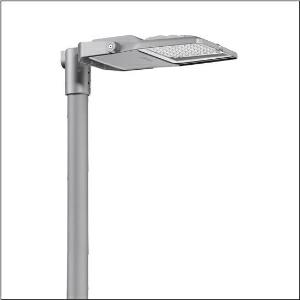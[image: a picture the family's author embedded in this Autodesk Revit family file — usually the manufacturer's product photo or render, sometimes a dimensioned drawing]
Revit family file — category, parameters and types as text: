
# Revit family: floodlight_fl_21_iq_mini___pl52_5xa7771b2d3a_cd8f
name_source: partatom
category: Lighting Fixtures
units: mm (PartAtom-declared; Revit-internal decimal feet)

## family parameters
Cut with Voids When Loaded = No
Host = Face
Light Source = No
Part Type = Normal
Room Calculation Point = No
Round Connector Dimension = Use Diameter
Shared = No

## types (1)
- --- (1 x LED, 6240 lm, 45.5 W, 3000K)
    Apparent Load = 46 VA
    CIE Flux Codes = 26 60 98 100 100
    Color Rendering = 70
    Color Temperature = 3000K
    Default Elevation = 1800 mm
    Description = Floodlight FL 21 iQ mini, floodlight, primary light control with lens, of PMMA, primary optical cover: protective disc, of toughened safety glass, transparent, light distribution: PL52, light emission: direct distribution, installation type: surface-mounted, LED, High Power LED, rated luminous flux: 6.240lm, luminous efficacy: 137lm/W, light colour: 730, colour temperature: 3000K, control: Auto-Match, Temp-Guard, Lumen-Switch, Night-Set, Smart-Wire, Light-Fading, Desk-Remote (wireless, voltage-free reading and setting of iQ features in the workshop via application-optimized NFC function/RFID function), optimised constant luminous flux control (CLO 2.0), with terminal, 6-pole, mains connection: 220..240V, AC, 50/60Hz, start of lifetime: 46W, end of service life: 48W, reduction: 22W, luminaire housing, of diecast aluminium, powder-coated, Siteco® metallic grey (DB 702S), corrosivity category C5 mid according to DIN EN ISO 12944, sealing non-destructively replaceable, please order mast flange separately, mast bracket, of steel, galvanised, powder-coated, Siteco® metallic grey (DB 702S), protection rating (complete): IP66, insulation class (complete): insulation class II (safety insulation), certification: CE, ENEC, VDE, protection symbol: D, impact resistance: IK08, permissible operating ambient temperature: -40..+40°C, permissible operating ambient temperature for outdoor applications: -40..+50°C, standard: DIN EN 12944, LABS conformity tested according to VDMA 24364:2018-05, packaging unit: 1 piece

Light Distribution: PL52
    Height = 70 mm
    Lamp = 1 x LED
    Lamp Light Flux = 6240 lm
    Lamp Power = 45.5 W
    Lamp count = 1
    Length = 485 mm
    Luminous efficacy = 137 lm/W
    Manufacturer = Siteco
    ModVariant = No
    Model = 5XA7771B2D3A
    Number of Poles = 1
    OnlyDefault = Yes
    Power Factor = 1
    Product Name = Floodlight FL 21 iQ mini | PL52
    Product group = floodlight | pylon annexe
    ProductGroupID = 6200
    Protection Class = Protection class II
    Protection Degree = IP 66
    RLX_Detail_Level = 1
    RLX_Emergency_Light_Flux = 0 lm
    RLX_Emergency_Type = 0
    RLX_Emergency_Type_DB = No
    RlxData = <blob elided: 101385 chars, md5=539fc8cc>
    Socket = socket
    Standby Power = 0 W
    System Light Flux = 6240 lm
    System Power = 46 W
    Type Comments = factory setting: luminous flux: 100 % | dim-lin: 254 | 463 mA
    Type Image = l_1007125.jpg
    URL = http://relux.com
    VarID = @adj_115247
    Voltage = 0 V
    Weight = 0.00 kg
    Width = 337 mm

## geometry (parser evidence)
native form markers: Blend x4, Sweep x13
no freeform markers — native parametric forms only
